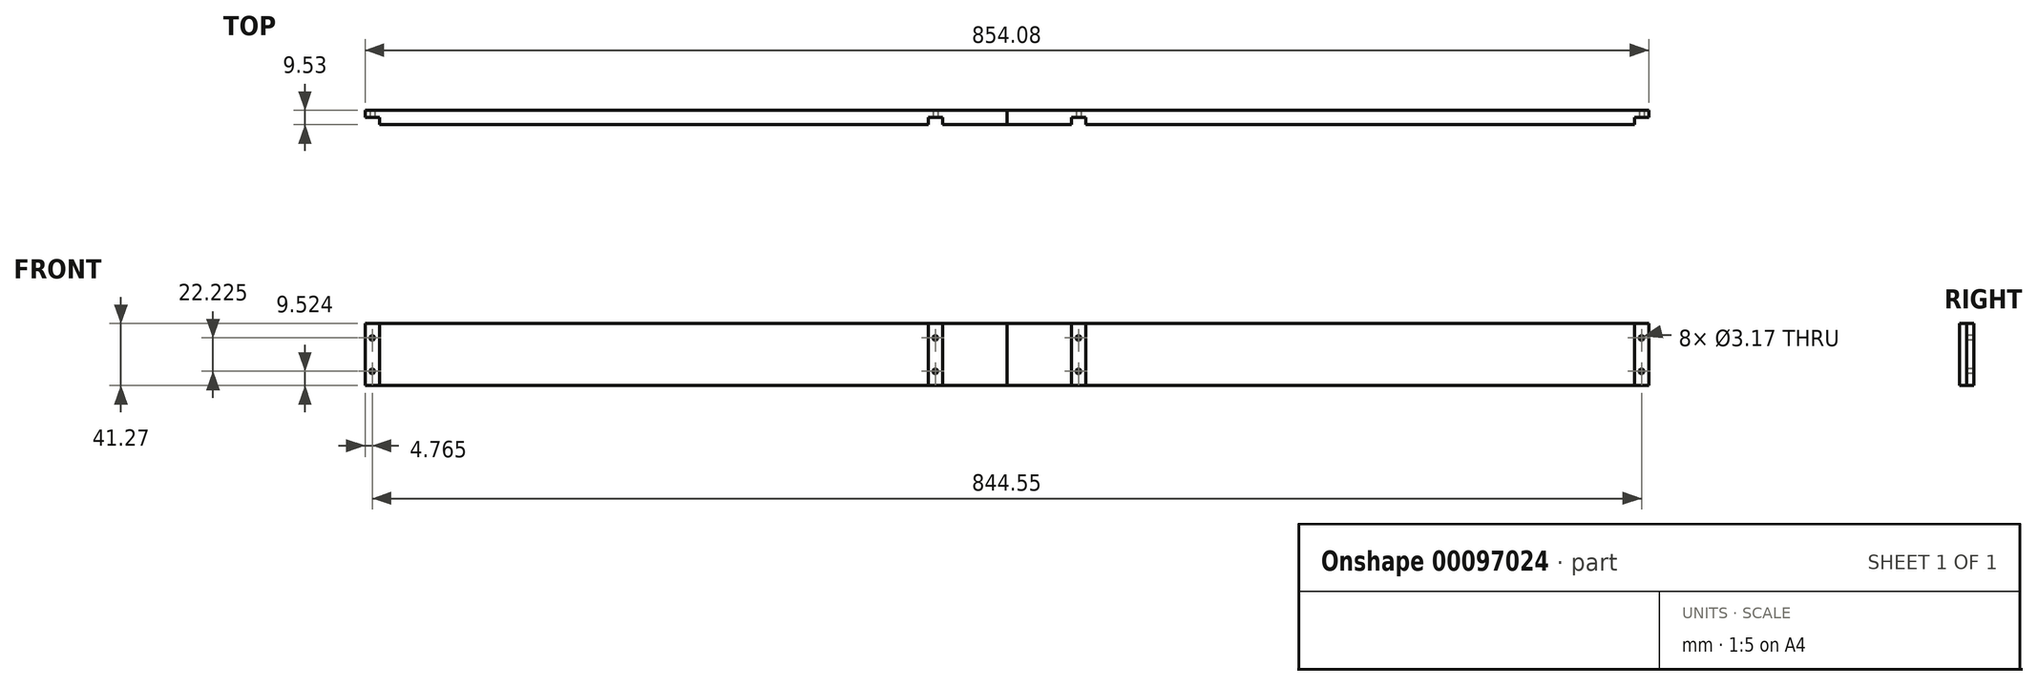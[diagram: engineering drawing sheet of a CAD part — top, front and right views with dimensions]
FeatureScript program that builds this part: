
annotation { "Feature Type Name" : "Feature", "Feature Type Description" : "" }
export const myFeature = defineFeature(function(context is Context, id is Id, definition is map)
    precondition{}
    {
        {
            var Q0;
            Q0=qCreatedBy(makeId("Front.planeOp"),FACE);
            var sketch = newSketch(context, id + "F0", { "sketchPlane" : qUnion([Q0])});
            skLineSegment(sketch, "E0", {"start": v(70.47, -5.54) * mm, "end": v(-356.57, -5.54) * mm});
            skLineSegment(sketch, "E1", {"start": v(-356.57, -5.54) * mm, "end": v(-356.57, 35.73) * mm});
            skLineSegment(sketch, "E2", {"start": v(-356.57, 35.73) * mm, "end": v(70.47, 35.73) * mm});
            skLineSegment(sketch, "E3", {"start": v(70.47, 35.73) * mm, "end": v(70.47, -5.54) * mm});
            skLineSegment(sketch, "E4.0", {"start": v(-313.7, -5.54) * mm, "end": v(-313.7, 35.73) * mm});
            skLineSegment(sketch, "E5.0", {"start": v(-304.18, -5.54) * mm, "end": v(-304.18, 35.73) * mm});
            skLineSegment(sketch, "E6.0", {"start": v(60.94, 35.73) * mm, "end": v(60.94, -5.54) * mm});
            skCircle(sketch, "E7", {"center": v(-308.94, 26.2) * mm, "radius": 1.59 * mm});
            skCircle(sketch, "E8.MirrorC", {"center": v(-308.94, 3.98) * mm, "radius": 1.59 * mm});
            skCircle(sketch, "E9.MirrorC", {"center": v(65.7, 3.98) * mm, "radius": 1.59 * mm});
            skCircle(sketch, "E10", {"center": v(65.7, 26.2) * mm, "radius": 1.59 * mm});
            skText(sketch, "E11", { "text": "3/8 inch Pine\n", "fontName": "OpenSans-Regular.ttf"});
            const initialGuessF0  = {"E11": [-0.21984, -0.06622, 1, 0, 0.0246]};
            skSetInitialGuess(sketch, initialGuessF0);
            skSolve(sketch);
        }
        {
            var Q0;
            {var subQ0=sQuery(id+"F0.wireOp",EDGE,"E1");Q0=makeQuery(id+"F0.imprint","IMPRINT",FACE,{"disambiguationData":[TD([[makeQuery(id+"F0.imprint","IMPRINT",EDGE,{"derivedFrom":subQ0}),-1.0]])]});}
            var Q1;
            {var subQ1=sQuery(id+"F0.wireOp",EDGE,"E4.0");Q1=makeQuery(id+"F0.imprint","IMPRINT",FACE,{"disambiguationData":[TD([[makeQuery(id+"F0.imprint","IMPRINT",EDGE,{"derivedFrom":subQ1}),-1.0]])]});}
            var Q2;
            {var subQ0=sQuery(id+"F0.wireOp",EDGE,"E5.0");Q2=makeQuery(id+"F0.imprint","IMPRINT",FACE,{"disambiguationData":[TD([[makeQuery(id+"F0.imprint","IMPRINT",EDGE,{"derivedFrom":subQ0}),-1.0]])]});}
            var Q3;
            {var subQ1=sQuery(id+"F0.wireOp",EDGE,"E3");Q3=makeQuery(id+"F0.imprint","IMPRINT",FACE,{"disambiguationData":[TD([[makeQuery(id+"F0.imprint","IMPRINT",EDGE,{"derivedFrom":subQ1}),-1.0]])]});}
            extrude(context, id + "F1", {"entities" : qUnion([Q0, Q1, Q2, Q3]), "oppositeDirection" : true, "depth" : 9.52 * mm});
        }
        {
            var Q0;
            {var subQ1=sQuery(id+"F0.wireOp",EDGE,"E3");Q0=makeQuery(id+"F0.imprint","IMPRINT",FACE,{"disambiguationData":[TD([[makeQuery(id+"F0.imprint","IMPRINT",EDGE,{"derivedFrom":subQ1}),-1.0]])]});}
            var Q1;
            {var subQ1=sQuery(id+"F0.wireOp",EDGE,"E4.0");Q1=makeQuery(id+"F0.imprint","IMPRINT",FACE,{"disambiguationData":[TD([[makeQuery(id+"F0.imprint","IMPRINT",EDGE,{"derivedFrom":subQ1}),-1.0]])]});}
            extrude(context, id + "F2", {"entities" : qUnion([Q0, Q1]), "operationType" : NewBodyOperationType.REMOVE, "oppositeDirection" : true, "depth" : 4.76 * mm});
        }
        {
            var Q0;
            Q0=makeQuery(id+"F1.opExtrude","SWEPT_BODY",BODY,{"disambiguationData":[OSD([sQuery(id+"F0.wireOp",EDGE,"E0"),sQuery(id+"F0.wireOp",EDGE,"E1"),sQuery(id+"F0.wireOp",EDGE,"E2"),sQuery(id+"F0.wireOp",EDGE,"E3"),sQuery(id+"F0.wireOp",EDGE,"E7"),sQuery(id+"F0.wireOp",EDGE,"E8.MirrorC"),sQuery(id+"F0.wireOp",EDGE,"E9.MirrorC"),sQuery(id+"F0.wireOp",EDGE,"E10")])]});
            var Q1;
            Q1=makeQuery(id+"F1.opExtrude","SWEPT_FACE",FACE,{"disambiguationData":[OSD([sQuery(id+"F0.wireOp",EDGE,"E1")])]});
            mirror(context, id + "F3", {"entities" : qUnion([Q0]), "mirrorPlane" : qUnion([Q1])});
        }
    });
